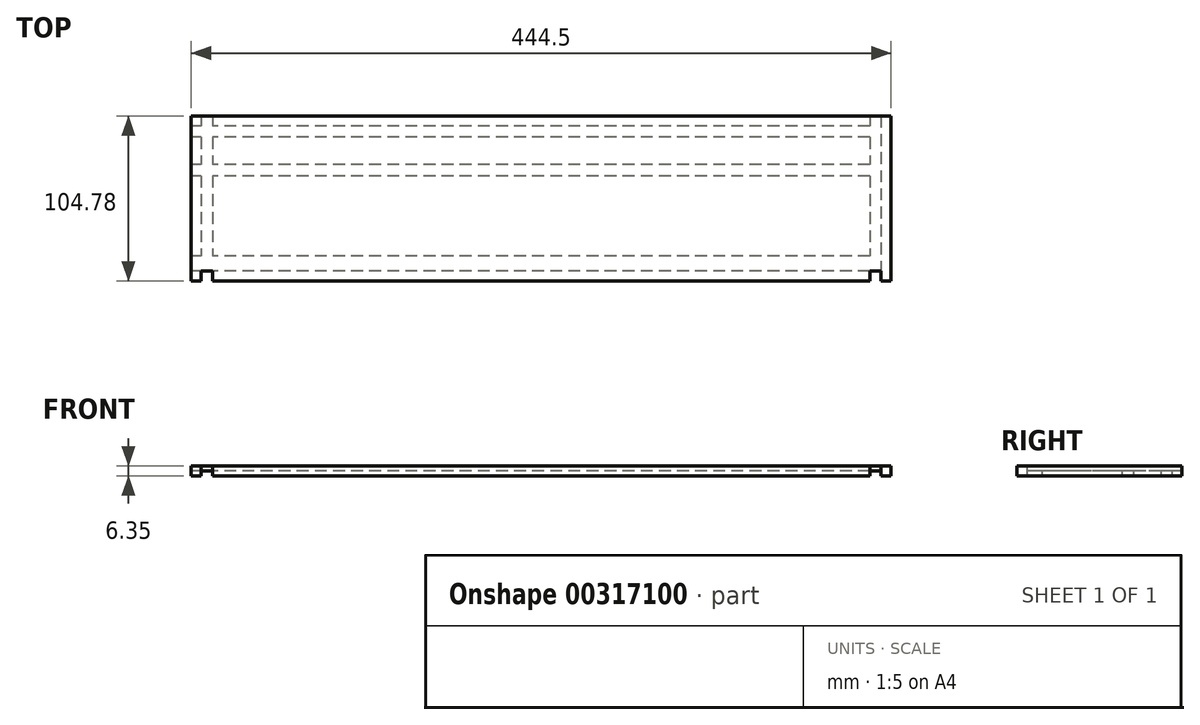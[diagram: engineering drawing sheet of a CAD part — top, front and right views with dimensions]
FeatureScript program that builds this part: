
annotation { "Feature Type Name" : "Feature", "Feature Type Description" : "" }
export const myFeature = defineFeature(function(context is Context, id is Id, definition is map)
    precondition{}
    {
        {
            var Q0;
            Q0=qCreatedBy(makeId("Top.planeOp"),FACE);
            var sketch = newSketch(context, id + "F0", { "sketchPlane" : qUnion([Q0])});
            skLineSegment(sketch, "E0.bottom", {"start": v(222.25, 52.39) * mm, "end": v(-222.25, 52.39) * mm});
            skLineSegment(sketch, "E0.top", {"start": v(222.25, -52.39) * mm, "end": v(-222.25, -52.39) * mm});
            skLineSegment(sketch, "E0.left", {"start": v(222.25, 52.39) * mm, "end": v(222.25, -52.39) * mm});
            skLineSegment(sketch, "E0.right", {"start": v(-222.25, 52.39) * mm, "end": v(-222.25, -52.39) * mm});
            skPoint(sketch, "E0.middle", {"position": v(0, 0) * mm});
            skLineSegment(sketch, "E1.0", {"start": v(-215.9, 52.39) * mm, "end": v(-215.9, -52.39) * mm});
            skLineSegment(sketch, "E2.0", {"start": v(-208.76, 52.39) * mm, "end": v(-208.76, -52.39) * mm});
            skLineSegment(sketch, "E3.0", {"start": v(215.9, 52.39) * mm, "end": v(215.9, -52.39) * mm});
            skLineSegment(sketch, "E4.0", {"start": v(208.76, 52.39) * mm, "end": v(208.76, -52.39) * mm});
            skLineSegment(sketch, "E5", {"start": v(215.9, -46.04) * mm, "end": v(-222.25, -46.04) * mm});
            skLineSegment(sketch, "E6.0", {"start": v(215.9, -36.51) * mm, "end": v(-222.25, -36.51) * mm});
            skLineSegment(sketch, "E7.0", {"start": v(215.9, 14.29) * mm, "end": v(-222.25, 14.29) * mm});
            skLineSegment(sketch, "E8.0", {"start": v(215.9, 21.43) * mm, "end": v(-222.25, 21.43) * mm});
            skLineSegment(sketch, "E9", {"start": v(215.9, 46.04) * mm, "end": v(-222.25, 46.04) * mm});
            skLineSegment(sketch, "E10.0", {"start": v(215.9, 38.9) * mm, "end": v(-222.25, 38.9) * mm});
            skSolve(sketch);
        }
        {
            var Q0;
            {var subQ0=sQuery(id+"F0.wireOp",EDGE,"E2.0");var subQ1=sQuery(id+"F0.wireOp",EDGE,"E0.bottom");var subQ2=makeQuery(id+"F0.imprint","INTERSECT",VERTEX,{"derivedFrom":[subQ1,subQ0]});Q0=makeQuery(id+"F0.imprint","IMPRINT",FACE,{"disambiguationData":[TD([[makeQuery(id+"F0.imprint","IMPRINT",EDGE,{"disambiguationData":[TD([[subQ2,1.0]])],"derivedFrom":subQ1}),1.0]])]});}
            var Q1;
            {var subQ0=sQuery(id+"F0.wireOp",EDGE,"E2.0");var subQ1=sQuery(id+"F0.wireOp",EDGE,"E0.top");var subQ2=makeQuery(id+"F0.imprint","INTERSECT",VERTEX,{"derivedFrom":[subQ1,subQ0]});Q1=makeQuery(id+"F0.imprint","IMPRINT",FACE,{"disambiguationData":[TD([[makeQuery(id+"F0.imprint","IMPRINT",EDGE,{"disambiguationData":[TD([[subQ2,1.0]])],"derivedFrom":subQ1}),-1.0]])]});}
            var Q2;
            {var subQ0=sQuery(id+"F0.wireOp",EDGE,"E7.0");var subQ1=sQuery(id+"F0.wireOp",EDGE,"E1.0");var subQ2=makeQuery(id+"F0.imprint","INTERSECT",VERTEX,{"derivedFrom":[subQ1,subQ0]});Q2=makeQuery(id+"F0.imprint","IMPRINT",FACE,{"disambiguationData":[TD([[makeQuery(id+"F0.imprint","IMPRINT",EDGE,{"disambiguationData":[TD([[subQ2,-1.0]])],"derivedFrom":subQ1}),1.0]])]});}
            var Q3;
            {var subQ0=sQuery(id+"F0.wireOp",EDGE,"E10.0");var subQ1=sQuery(id+"F0.wireOp",EDGE,"E1.0");var subQ2=makeQuery(id+"F0.imprint","INTERSECT",VERTEX,{"derivedFrom":[subQ1,subQ0]});Q3=makeQuery(id+"F0.imprint","IMPRINT",FACE,{"disambiguationData":[TD([[makeQuery(id+"F0.imprint","IMPRINT",EDGE,{"disambiguationData":[TD([[subQ2,-1.0]])],"derivedFrom":subQ1}),1.0]])]});}
            var Q4;
            {var subQ0=sQuery(id+"F0.wireOp",EDGE,"E9");var subQ1=sQuery(id+"F0.wireOp",EDGE,"E2.0");var subQ2=makeQuery(id+"F0.imprint","INTERSECT",VERTEX,{"derivedFrom":[subQ1,subQ0]});Q4=makeQuery(id+"F0.imprint","IMPRINT",FACE,{"disambiguationData":[TD([[makeQuery(id+"F0.imprint","IMPRINT",EDGE,{"disambiguationData":[TD([[subQ2,-1.0]])],"derivedFrom":subQ1}),1.0]])]});}
            var Q5;
            {var subQ0=sQuery(id+"F0.wireOp",EDGE,"E8.0");var subQ1=sQuery(id+"F0.wireOp",EDGE,"E2.0");var subQ2=makeQuery(id+"F0.imprint","INTERSECT",VERTEX,{"derivedFrom":[subQ1,subQ0]});Q5=makeQuery(id+"F0.imprint","IMPRINT",FACE,{"disambiguationData":[TD([[makeQuery(id+"F0.imprint","IMPRINT",EDGE,{"disambiguationData":[TD([[subQ2,-1.0]])],"derivedFrom":subQ1}),1.0]])]});}
            var Q6;
            {var subQ4=sQuery(id+"F0.wireOp",EDGE,"E0.left");Q6=makeQuery(id+"F0.imprint","IMPRINT",FACE,{"disambiguationData":[TD([[makeQuery(id+"F0.imprint","IMPRINT",EDGE,{"derivedFrom":subQ4}),-1.0]])]});}
            var Q7;
            {var subQ0=sQuery(id+"F0.wireOp",EDGE,"E6.0");var subQ1=sQuery(id+"F0.wireOp",EDGE,"E0.right");var subQ2=makeQuery(id+"F0.imprint","INTERSECT",VERTEX,{"derivedFrom":[subQ1,subQ0]});Q7=makeQuery(id+"F0.imprint","IMPRINT",FACE,{"disambiguationData":[TD([[makeQuery(id+"F0.imprint","IMPRINT",EDGE,{"disambiguationData":[TD([[subQ2,1.0]])],"derivedFrom":subQ1}),1.0]])]});}
            var Q8;
            {var subQ0=sQuery(id+"F0.wireOp",EDGE,"E6.0");var subQ1=sQuery(id+"F0.wireOp",EDGE,"E2.0");var subQ2=makeQuery(id+"F0.imprint","INTERSECT",VERTEX,{"derivedFrom":[subQ1,subQ0]});Q8=makeQuery(id+"F0.imprint","IMPRINT",FACE,{"disambiguationData":[TD([[makeQuery(id+"F0.imprint","IMPRINT",EDGE,{"disambiguationData":[TD([[subQ2,-1.0]])],"derivedFrom":subQ1}),1.0]])]});}
            var Q9;
            {var subQ0=sQuery(id+"F0.wireOp",EDGE,"E7.0");var subQ1=sQuery(id+"F0.wireOp",EDGE,"E2.0");var subQ2=makeQuery(id+"F0.imprint","INTERSECT",VERTEX,{"derivedFrom":[subQ1,subQ0]});Q9=makeQuery(id+"F0.imprint","IMPRINT",FACE,{"disambiguationData":[TD([[makeQuery(id+"F0.imprint","IMPRINT",EDGE,{"disambiguationData":[TD([[subQ2,-1.0]])],"derivedFrom":subQ1}),1.0]])]});}
            var Q10;
            {var subQ0=sQuery(id+"F0.wireOp",EDGE,"E10.0");var subQ1=sQuery(id+"F0.wireOp",EDGE,"E2.0");var subQ2=makeQuery(id+"F0.imprint","INTERSECT",VERTEX,{"derivedFrom":[subQ1,subQ0]});Q10=makeQuery(id+"F0.imprint","IMPRINT",FACE,{"disambiguationData":[TD([[makeQuery(id+"F0.imprint","IMPRINT",EDGE,{"disambiguationData":[TD([[subQ2,-1.0]])],"derivedFrom":subQ1}),1.0]])]});}
            var Q11;
            {var subQ0=sQuery(id+"F0.wireOp",EDGE,"E9");var subQ1=sQuery(id+"F0.wireOp",EDGE,"E0.right");var subQ2=makeQuery(id+"F0.imprint","INTERSECT",VERTEX,{"derivedFrom":[subQ1,subQ0]});Q11=makeQuery(id+"F0.imprint","IMPRINT",FACE,{"disambiguationData":[TD([[makeQuery(id+"F0.imprint","IMPRINT",EDGE,{"disambiguationData":[TD([[subQ2,-1.0]])],"derivedFrom":subQ1}),1.0]])]});}
            var Q12;
            {var subQ0=sQuery(id+"F0.wireOp",EDGE,"E1.0");var subQ1=sQuery(id+"F0.wireOp",EDGE,"E0.bottom");var subQ2=makeQuery(id+"F0.imprint","INTERSECT",VERTEX,{"derivedFrom":[subQ1,subQ0]});Q12=makeQuery(id+"F0.imprint","IMPRINT",FACE,{"disambiguationData":[TD([[makeQuery(id+"F0.imprint","IMPRINT",EDGE,{"disambiguationData":[TD([[subQ2,1.0]])],"derivedFrom":subQ1}),1.0]])]});}
            var Q13;
            {var subQ0=sQuery(id+"F0.wireOp",EDGE,"E3.0");var subQ1=sQuery(id+"F0.wireOp",EDGE,"E0.bottom");var subQ2=makeQuery(id+"F0.imprint","INTERSECT",VERTEX,{"derivedFrom":[subQ1,subQ0]});Q13=makeQuery(id+"F0.imprint","IMPRINT",FACE,{"disambiguationData":[TD([[makeQuery(id+"F0.imprint","IMPRINT",EDGE,{"disambiguationData":[TD([[subQ2,-1.0]])],"derivedFrom":subQ1}),1.0]])]});}
            var Q14;
            {var subQ0=sQuery(id+"F0.wireOp",EDGE,"E0.right");var subQ1=sQuery(id+"F0.wireOp",EDGE,"E0.bottom");var subQ2=makeQuery(id+"F0.imprint","INTERSECT",VERTEX,{"derivedFrom":[subQ1,subQ0]});Q14=makeQuery(id+"F0.imprint","IMPRINT",FACE,{"disambiguationData":[TD([[makeQuery(id+"F0.imprint","IMPRINT",EDGE,{"disambiguationData":[TD([[subQ2,1.0]])],"derivedFrom":subQ1}),1.0]])]});}
            var Q15;
            {var subQ0=sQuery(id+"F0.wireOp",EDGE,"E8.0");var subQ1=sQuery(id+"F0.wireOp",EDGE,"E1.0");var subQ2=makeQuery(id+"F0.imprint","INTERSECT",VERTEX,{"derivedFrom":[subQ1,subQ0]});Q15=makeQuery(id+"F0.imprint","IMPRINT",FACE,{"disambiguationData":[TD([[makeQuery(id+"F0.imprint","IMPRINT",EDGE,{"disambiguationData":[TD([[subQ2,-1.0]])],"derivedFrom":subQ1}),1.0]])]});}
            var Q16;
            {var subQ0=sQuery(id+"F0.wireOp",EDGE,"E9");var subQ1=sQuery(id+"F0.wireOp",EDGE,"E1.0");var subQ2=makeQuery(id+"F0.imprint","INTERSECT",VERTEX,{"derivedFrom":[subQ1,subQ0]});Q16=makeQuery(id+"F0.imprint","IMPRINT",FACE,{"disambiguationData":[TD([[makeQuery(id+"F0.imprint","IMPRINT",EDGE,{"disambiguationData":[TD([[subQ2,-1.0]])],"derivedFrom":subQ1}),1.0]])]});}
            var Q17;
            {var subQ0=sQuery(id+"F0.wireOp",EDGE,"E8.0");var subQ1=sQuery(id+"F0.wireOp",EDGE,"E3.0");var subQ2=makeQuery(id+"F0.imprint","INTERSECT",VERTEX,{"derivedFrom":[subQ1,subQ0]});Q17=makeQuery(id+"F0.imprint","IMPRINT",FACE,{"disambiguationData":[TD([[makeQuery(id+"F0.imprint","IMPRINT",EDGE,{"disambiguationData":[TD([[subQ2,1.0]])],"derivedFrom":subQ1}),-1.0]])]});}
            var Q18;
            {var subQ0=sQuery(id+"F0.wireOp",EDGE,"E8.0");var subQ1=sQuery(id+"F0.wireOp",EDGE,"E0.right");var subQ2=makeQuery(id+"F0.imprint","INTERSECT",VERTEX,{"derivedFrom":[subQ1,subQ0]});Q18=makeQuery(id+"F0.imprint","IMPRINT",FACE,{"disambiguationData":[TD([[makeQuery(id+"F0.imprint","IMPRINT",EDGE,{"disambiguationData":[TD([[subQ2,1.0]])],"derivedFrom":subQ1}),1.0]])]});}
            var Q19;
            {var subQ0=sQuery(id+"F0.wireOp",EDGE,"E7.0");var subQ1=sQuery(id+"F0.wireOp",EDGE,"E0.right");var subQ2=makeQuery(id+"F0.imprint","INTERSECT",VERTEX,{"derivedFrom":[subQ1,subQ0]});Q19=makeQuery(id+"F0.imprint","IMPRINT",FACE,{"disambiguationData":[TD([[makeQuery(id+"F0.imprint","IMPRINT",EDGE,{"disambiguationData":[TD([[subQ2,1.0]])],"derivedFrom":subQ1}),1.0]])]});}
            var Q20;
            {var subQ0=sQuery(id+"F0.wireOp",EDGE,"E5");var subQ1=sQuery(id+"F0.wireOp",EDGE,"E0.right");var subQ2=makeQuery(id+"F0.imprint","INTERSECT",VERTEX,{"derivedFrom":[subQ1,subQ0]});Q20=makeQuery(id+"F0.imprint","IMPRINT",FACE,{"disambiguationData":[TD([[makeQuery(id+"F0.imprint","IMPRINT",EDGE,{"disambiguationData":[TD([[subQ2,1.0]])],"derivedFrom":subQ1}),1.0]])]});}
            var Q21;
            {var subQ0=sQuery(id+"F0.wireOp",EDGE,"E5");var subQ1=sQuery(id+"F0.wireOp",EDGE,"E3.0");var subQ2=makeQuery(id+"F0.imprint","INTERSECT",VERTEX,{"derivedFrom":[subQ1,subQ0]});Q21=makeQuery(id+"F0.imprint","IMPRINT",FACE,{"disambiguationData":[TD([[makeQuery(id+"F0.imprint","IMPRINT",EDGE,{"disambiguationData":[TD([[subQ2,1.0]])],"derivedFrom":subQ1}),-1.0]])]});}
            var Q22;
            {var subQ0=sQuery(id+"F0.wireOp",EDGE,"E9");var subQ1=sQuery(id+"F0.wireOp",EDGE,"E3.0");var subQ2=makeQuery(id+"F0.imprint","INTERSECT",VERTEX,{"derivedFrom":[subQ1,subQ0]});Q22=makeQuery(id+"F0.imprint","IMPRINT",FACE,{"disambiguationData":[TD([[makeQuery(id+"F0.imprint","IMPRINT",EDGE,{"disambiguationData":[TD([[subQ2,-1.0]])],"derivedFrom":subQ1}),-1.0]])]});}
            var Q23;
            {var subQ0=sQuery(id+"F0.wireOp",EDGE,"E7.0");var subQ1=sQuery(id+"F0.wireOp",EDGE,"E3.0");var subQ2=makeQuery(id+"F0.imprint","INTERSECT",VERTEX,{"derivedFrom":[subQ1,subQ0]});Q23=makeQuery(id+"F0.imprint","IMPRINT",FACE,{"disambiguationData":[TD([[makeQuery(id+"F0.imprint","IMPRINT",EDGE,{"disambiguationData":[TD([[subQ2,1.0]])],"derivedFrom":subQ1}),-1.0]])]});}
            var Q24;
            {var subQ0=sQuery(id+"F0.wireOp",EDGE,"E6.0");var subQ1=sQuery(id+"F0.wireOp",EDGE,"E1.0");var subQ2=makeQuery(id+"F0.imprint","INTERSECT",VERTEX,{"derivedFrom":[subQ1,subQ0]});Q24=makeQuery(id+"F0.imprint","IMPRINT",FACE,{"disambiguationData":[TD([[makeQuery(id+"F0.imprint","IMPRINT",EDGE,{"disambiguationData":[TD([[subQ2,-1.0]])],"derivedFrom":subQ1}),1.0]])]});}
            var Q25;
            {var subQ0=sQuery(id+"F0.wireOp",EDGE,"E0.right");var subQ1=sQuery(id+"F0.wireOp",EDGE,"E0.top");var subQ2=makeQuery(id+"F0.imprint","INTERSECT",VERTEX,{"derivedFrom":[subQ1,subQ0]});Q25=makeQuery(id+"F0.imprint","IMPRINT",FACE,{"disambiguationData":[TD([[makeQuery(id+"F0.imprint","IMPRINT",EDGE,{"disambiguationData":[TD([[subQ2,1.0]])],"derivedFrom":subQ1}),-1.0]])]});}
            var Q26;
            {var subQ0=sQuery(id+"F0.wireOp",EDGE,"E6.0");var subQ1=sQuery(id+"F0.wireOp",EDGE,"E3.0");var subQ2=makeQuery(id+"F0.imprint","INTERSECT",VERTEX,{"derivedFrom":[subQ1,subQ0]});Q26=makeQuery(id+"F0.imprint","IMPRINT",FACE,{"disambiguationData":[TD([[makeQuery(id+"F0.imprint","IMPRINT",EDGE,{"disambiguationData":[TD([[subQ2,1.0]])],"derivedFrom":subQ1}),-1.0]])]});}
            var Q27;
            Q27=sQuery(id+"F0.wireOp",EDGE,"E0.right");
            var Q28;
            Q28=sQuery(id+"F0.wireOp",EDGE,"E0.bottom");
            var Q29;
            Q29=sQuery(id+"F0.wireOp",EDGE,"E0.top");
            var Q30;
            Q30=sQuery(id+"F0.wireOp",EDGE,"E0.left");
            extrude(context, id + "F1", {"entities" : qUnion([Q0, Q1, Q2, Q3, Q4, Q5, Q6, Q7, Q8, Q9, Q10, Q11, Q12, Q13, Q14, Q15, Q16, Q17, Q18, Q19, Q20, Q21, Q22, Q23, Q24, Q25, Q26]), "surfaceEntities" : qUnion([Q27, Q28, Q29, Q30]), "depth" : 6.35 * mm});
        }
        {
            var Q0;
            {var subQ0=sQuery(id+"F0.wireOp",EDGE,"E6.0");var subQ1=sQuery(id+"F0.wireOp",EDGE,"E1.0");var subQ2=makeQuery(id+"F0.imprint","INTERSECT",VERTEX,{"derivedFrom":[subQ1,subQ0]});Q0=makeQuery(id+"F0.imprint","IMPRINT",FACE,{"disambiguationData":[TD([[makeQuery(id+"F0.imprint","IMPRINT",EDGE,{"disambiguationData":[TD([[subQ2,-1.0]])],"derivedFrom":subQ1}),1.0]])]});}
            var Q1;
            {var subQ0=sQuery(id+"F0.wireOp",EDGE,"E7.0");var subQ1=sQuery(id+"F0.wireOp",EDGE,"E1.0");var subQ2=makeQuery(id+"F0.imprint","INTERSECT",VERTEX,{"derivedFrom":[subQ1,subQ0]});Q1=makeQuery(id+"F0.imprint","IMPRINT",FACE,{"disambiguationData":[TD([[makeQuery(id+"F0.imprint","IMPRINT",EDGE,{"disambiguationData":[TD([[subQ2,-1.0]])],"derivedFrom":subQ1}),1.0]])]});}
            var Q2;
            {var subQ0=sQuery(id+"F0.wireOp",EDGE,"E8.0");var subQ1=sQuery(id+"F0.wireOp",EDGE,"E1.0");var subQ2=makeQuery(id+"F0.imprint","INTERSECT",VERTEX,{"derivedFrom":[subQ1,subQ0]});Q2=makeQuery(id+"F0.imprint","IMPRINT",FACE,{"disambiguationData":[TD([[makeQuery(id+"F0.imprint","IMPRINT",EDGE,{"disambiguationData":[TD([[subQ2,-1.0]])],"derivedFrom":subQ1}),1.0]])]});}
            var Q3;
            {var subQ0=sQuery(id+"F0.wireOp",EDGE,"E10.0");var subQ1=sQuery(id+"F0.wireOp",EDGE,"E1.0");var subQ2=makeQuery(id+"F0.imprint","INTERSECT",VERTEX,{"derivedFrom":[subQ1,subQ0]});Q3=makeQuery(id+"F0.imprint","IMPRINT",FACE,{"disambiguationData":[TD([[makeQuery(id+"F0.imprint","IMPRINT",EDGE,{"disambiguationData":[TD([[subQ2,-1.0]])],"derivedFrom":subQ1}),1.0]])]});}
            var Q4;
            {var subQ0=sQuery(id+"F0.wireOp",EDGE,"E9");var subQ1=sQuery(id+"F0.wireOp",EDGE,"E1.0");var subQ2=makeQuery(id+"F0.imprint","INTERSECT",VERTEX,{"derivedFrom":[subQ1,subQ0]});Q4=makeQuery(id+"F0.imprint","IMPRINT",FACE,{"disambiguationData":[TD([[makeQuery(id+"F0.imprint","IMPRINT",EDGE,{"disambiguationData":[TD([[subQ2,-1.0]])],"derivedFrom":subQ1}),1.0]])]});}
            var Q5;
            {var subQ0=sQuery(id+"F0.wireOp",EDGE,"E1.0");var subQ1=sQuery(id+"F0.wireOp",EDGE,"E0.bottom");var subQ2=makeQuery(id+"F0.imprint","INTERSECT",VERTEX,{"derivedFrom":[subQ1,subQ0]});Q5=makeQuery(id+"F0.imprint","IMPRINT",FACE,{"disambiguationData":[TD([[makeQuery(id+"F0.imprint","IMPRINT",EDGE,{"disambiguationData":[TD([[subQ2,1.0]])],"derivedFrom":subQ1}),1.0]])]});}
            var Q6;
            {var subQ0=sQuery(id+"F0.wireOp",EDGE,"E9");var subQ1=sQuery(id+"F0.wireOp",EDGE,"E0.right");var subQ2=makeQuery(id+"F0.imprint","INTERSECT",VERTEX,{"derivedFrom":[subQ1,subQ0]});Q6=makeQuery(id+"F0.imprint","IMPRINT",FACE,{"disambiguationData":[TD([[makeQuery(id+"F0.imprint","IMPRINT",EDGE,{"disambiguationData":[TD([[subQ2,-1.0]])],"derivedFrom":subQ1}),1.0]])]});}
            var Q7;
            {var subQ0=sQuery(id+"F0.wireOp",EDGE,"E7.0");var subQ1=sQuery(id+"F0.wireOp",EDGE,"E0.right");var subQ2=makeQuery(id+"F0.imprint","INTERSECT",VERTEX,{"derivedFrom":[subQ1,subQ0]});Q7=makeQuery(id+"F0.imprint","IMPRINT",FACE,{"disambiguationData":[TD([[makeQuery(id+"F0.imprint","IMPRINT",EDGE,{"disambiguationData":[TD([[subQ2,1.0]])],"derivedFrom":subQ1}),1.0]])]});}
            var Q8;
            {var subQ0=sQuery(id+"F0.wireOp",EDGE,"E8.0");var subQ1=sQuery(id+"F0.wireOp",EDGE,"E2.0");var subQ2=makeQuery(id+"F0.imprint","INTERSECT",VERTEX,{"derivedFrom":[subQ1,subQ0]});Q8=makeQuery(id+"F0.imprint","IMPRINT",FACE,{"disambiguationData":[TD([[makeQuery(id+"F0.imprint","IMPRINT",EDGE,{"disambiguationData":[TD([[subQ2,-1.0]])],"derivedFrom":subQ1}),1.0]])]});}
            var Q9;
            {var subQ0=sQuery(id+"F0.wireOp",EDGE,"E9");var subQ1=sQuery(id+"F0.wireOp",EDGE,"E2.0");var subQ2=makeQuery(id+"F0.imprint","INTERSECT",VERTEX,{"derivedFrom":[subQ1,subQ0]});Q9=makeQuery(id+"F0.imprint","IMPRINT",FACE,{"disambiguationData":[TD([[makeQuery(id+"F0.imprint","IMPRINT",EDGE,{"disambiguationData":[TD([[subQ2,-1.0]])],"derivedFrom":subQ1}),1.0]])]});}
            var Q10;
            {var subQ0=sQuery(id+"F0.wireOp",EDGE,"E5");var subQ1=sQuery(id+"F0.wireOp",EDGE,"E0.right");var subQ2=makeQuery(id+"F0.imprint","INTERSECT",VERTEX,{"derivedFrom":[subQ1,subQ0]});Q10=makeQuery(id+"F0.imprint","IMPRINT",FACE,{"disambiguationData":[TD([[makeQuery(id+"F0.imprint","IMPRINT",EDGE,{"disambiguationData":[TD([[subQ2,1.0]])],"derivedFrom":subQ1}),1.0]])]});}
            var Q11;
            {var subQ0=sQuery(id+"F0.wireOp",EDGE,"E6.0");var subQ1=sQuery(id+"F0.wireOp",EDGE,"E2.0");var subQ2=makeQuery(id+"F0.imprint","INTERSECT",VERTEX,{"derivedFrom":[subQ1,subQ0]});Q11=makeQuery(id+"F0.imprint","IMPRINT",FACE,{"disambiguationData":[TD([[makeQuery(id+"F0.imprint","IMPRINT",EDGE,{"disambiguationData":[TD([[subQ2,-1.0]])],"derivedFrom":subQ1}),1.0]])]});}
            var Q12;
            {var subQ0=sQuery(id+"F0.wireOp",EDGE,"E5");var subQ1=sQuery(id+"F0.wireOp",EDGE,"E3.0");var subQ2=makeQuery(id+"F0.imprint","INTERSECT",VERTEX,{"derivedFrom":[subQ1,subQ0]});Q12=makeQuery(id+"F0.imprint","IMPRINT",FACE,{"disambiguationData":[TD([[makeQuery(id+"F0.imprint","IMPRINT",EDGE,{"disambiguationData":[TD([[subQ2,1.0]])],"derivedFrom":subQ1}),-1.0]])]});}
            var Q13;
            {var subQ0=sQuery(id+"F0.wireOp",EDGE,"E7.0");var subQ1=sQuery(id+"F0.wireOp",EDGE,"E3.0");var subQ2=makeQuery(id+"F0.imprint","INTERSECT",VERTEX,{"derivedFrom":[subQ1,subQ0]});Q13=makeQuery(id+"F0.imprint","IMPRINT",FACE,{"disambiguationData":[TD([[makeQuery(id+"F0.imprint","IMPRINT",EDGE,{"disambiguationData":[TD([[subQ2,1.0]])],"derivedFrom":subQ1}),-1.0]])]});}
            var Q14;
            {var subQ0=sQuery(id+"F0.wireOp",EDGE,"E9");var subQ1=sQuery(id+"F0.wireOp",EDGE,"E3.0");var subQ2=makeQuery(id+"F0.imprint","INTERSECT",VERTEX,{"derivedFrom":[subQ1,subQ0]});Q14=makeQuery(id+"F0.imprint","IMPRINT",FACE,{"disambiguationData":[TD([[makeQuery(id+"F0.imprint","IMPRINT",EDGE,{"disambiguationData":[TD([[subQ2,-1.0]])],"derivedFrom":subQ1}),-1.0]])]});}
            var Q15;
            {var subQ0=sQuery(id+"F0.wireOp",EDGE,"E3.0");var subQ1=sQuery(id+"F0.wireOp",EDGE,"E0.bottom");var subQ2=makeQuery(id+"F0.imprint","INTERSECT",VERTEX,{"derivedFrom":[subQ1,subQ0]});Q15=makeQuery(id+"F0.imprint","IMPRINT",FACE,{"disambiguationData":[TD([[makeQuery(id+"F0.imprint","IMPRINT",EDGE,{"disambiguationData":[TD([[subQ2,-1.0]])],"derivedFrom":subQ1}),1.0]])]});}
            var Q16;
            {var subQ0=sQuery(id+"F0.wireOp",EDGE,"E8.0");var subQ1=sQuery(id+"F0.wireOp",EDGE,"E3.0");var subQ2=makeQuery(id+"F0.imprint","INTERSECT",VERTEX,{"derivedFrom":[subQ1,subQ0]});Q16=makeQuery(id+"F0.imprint","IMPRINT",FACE,{"disambiguationData":[TD([[makeQuery(id+"F0.imprint","IMPRINT",EDGE,{"disambiguationData":[TD([[subQ2,1.0]])],"derivedFrom":subQ1}),-1.0]])]});}
            var Q17;
            {var subQ0=sQuery(id+"F0.wireOp",EDGE,"E6.0");var subQ1=sQuery(id+"F0.wireOp",EDGE,"E3.0");var subQ2=makeQuery(id+"F0.imprint","INTERSECT",VERTEX,{"derivedFrom":[subQ1,subQ0]});Q17=makeQuery(id+"F0.imprint","IMPRINT",FACE,{"disambiguationData":[TD([[makeQuery(id+"F0.imprint","IMPRINT",EDGE,{"disambiguationData":[TD([[subQ2,1.0]])],"derivedFrom":subQ1}),-1.0]])]});}
            extrude(context, id + "F2", {"entities" : qUnion([Q0, Q1, Q2, Q3, Q4, Q5, Q6, Q7, Q8, Q9, Q10, Q11, Q12, Q13, Q14, Q15, Q16, Q17]), "operationType" : NewBodyOperationType.REMOVE, "depth" : 3.17 * mm});
        }
    });
